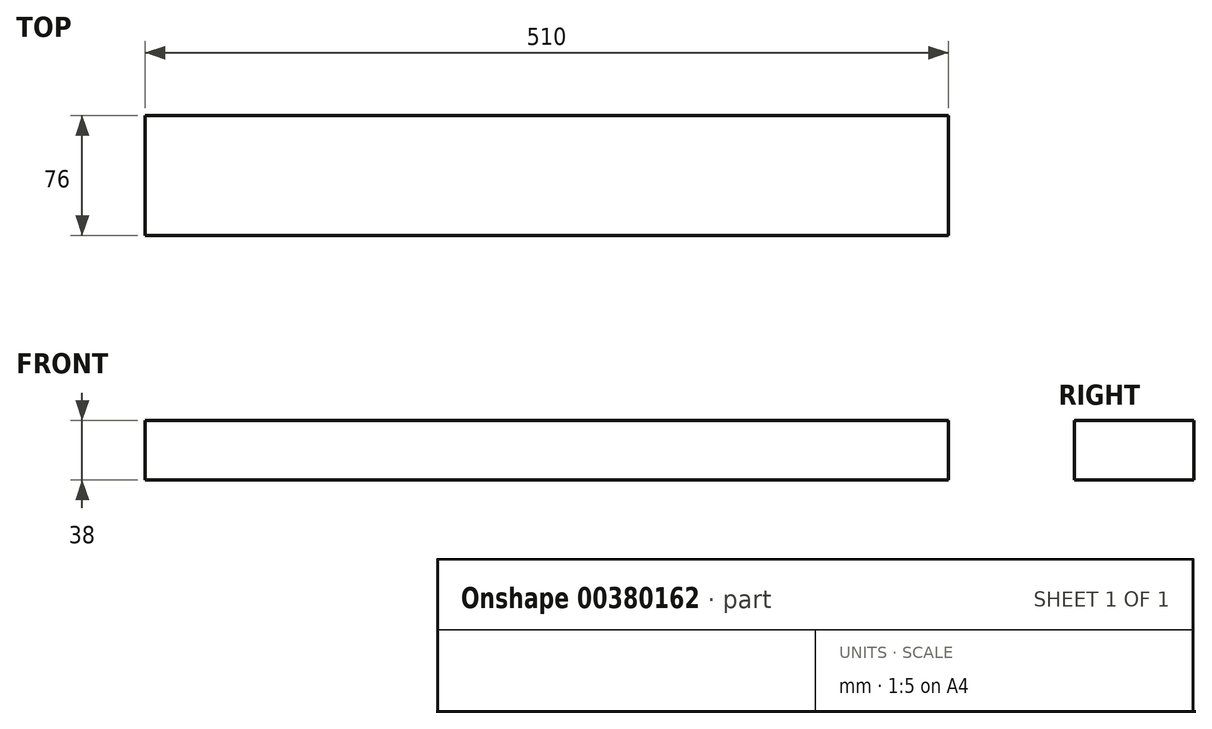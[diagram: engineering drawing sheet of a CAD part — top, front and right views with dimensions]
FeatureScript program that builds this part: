
annotation { "Feature Type Name" : "Feature", "Feature Type Description" : "" }
export const myFeature = defineFeature(function(context is Context, id is Id, definition is map)
    precondition{}
    {
        {
            var Q0;
            Q0=qCreatedBy(makeId("Right.planeOp"),FACE);
            var sketch = newSketch(context, id + "F0", { "sketchPlane" : qUnion([Q0])});
            skLineSegment(sketch, "E0.bottom", {"start": v(-38, -19) * mm, "end": v(38, -19) * mm});
            skLineSegment(sketch, "E0.top", {"start": v(-38, 19) * mm, "end": v(38, 19) * mm});
            skLineSegment(sketch, "E0.left", {"start": v(-38, -19) * mm, "end": v(-38, 19) * mm});
            skLineSegment(sketch, "E0.right", {"start": v(38, -19) * mm, "end": v(38, 19) * mm});
            skPoint(sketch, "E0.middle", {"position": v(0, 0) * mm});
            skSolve(sketch);
        }
        {
            var Q0;
            Q0 = qSketchRegion(id + "F0", true);
            extrude(context, id + "F1", {"entities" : qUnion([Q0]), "depth" : 510 * mm});
        }
    });
